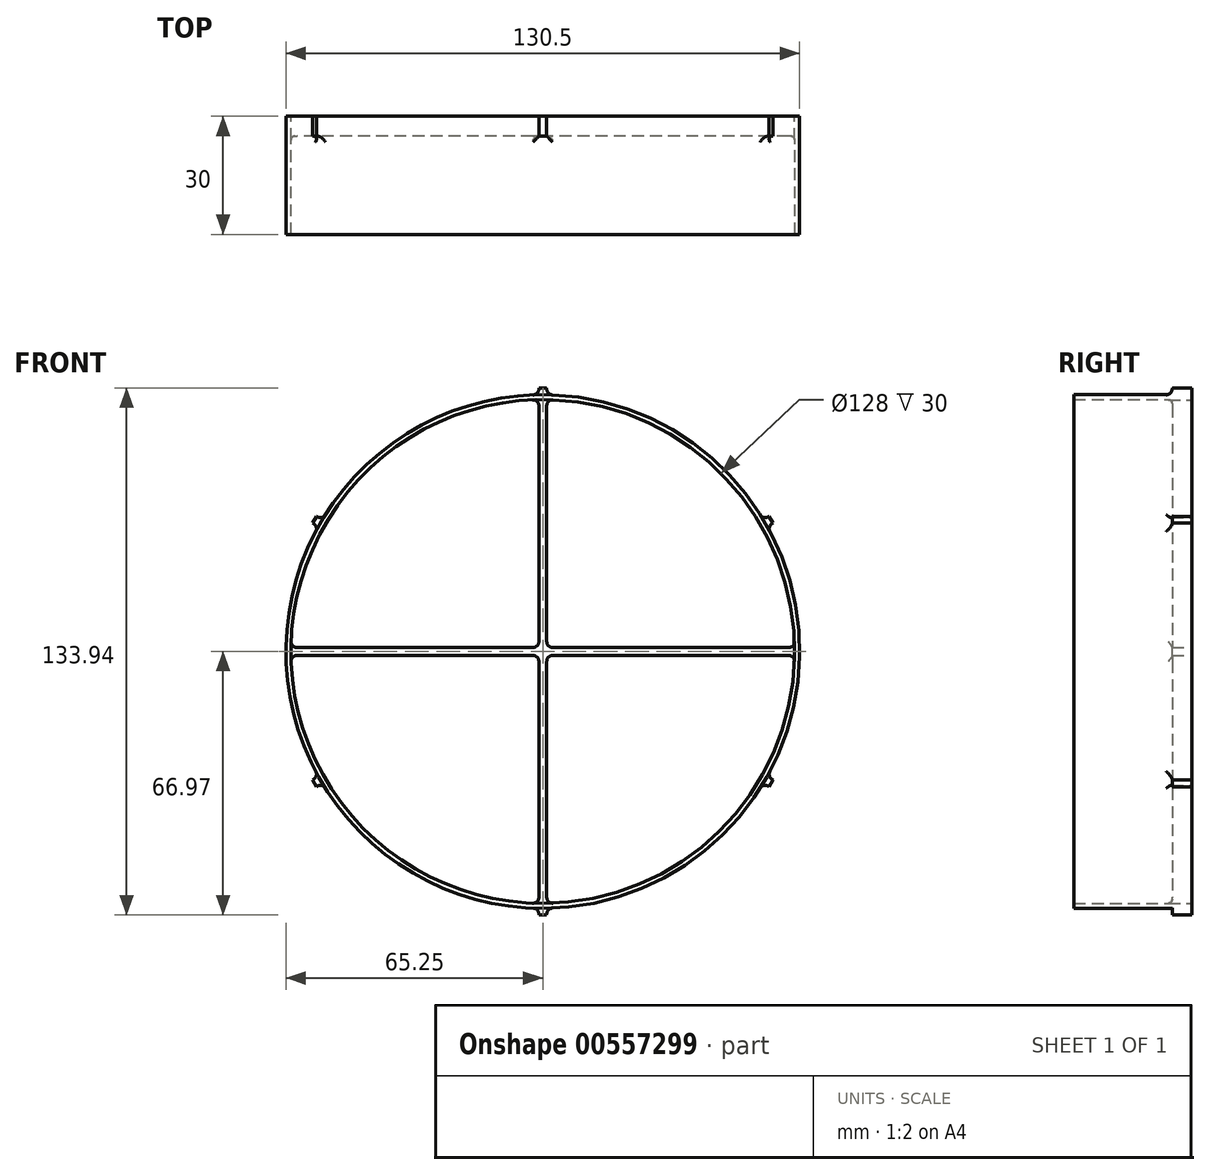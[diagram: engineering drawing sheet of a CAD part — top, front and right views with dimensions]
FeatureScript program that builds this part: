
annotation { "Feature Type Name" : "Feature", "Feature Type Description" : "" }
export const myFeature = defineFeature(function(context is Context, id is Id, definition is map)
    precondition{}
    {
        {
            var Q0;
            Q0=qCreatedBy(makeId("Front.planeOp"),FACE);
            var sketch = newSketch(context, id + "F0", { "sketchPlane" : qUnion([Q0])});
            skArc(sketch, "E0", {"start": v(64, 1) * mm, "mid": v(45.25, 45.25) * mm, "end": v(1, 64) * mm});
            skCircle(sketch, "E1", {"center": v(0, 0) * mm, "radius": 65.25 * mm});
            skLineSegment(sketch, "E2", {"start": v(0, 0) * mm, "end": v(0, 65.25) * mm, "construction": true});
            skLineSegment(sketch, "E3", {"start": v(0, 65.25) * mm, "end": v(0, -65.25) * mm, "construction": true});
            skLineSegment(sketch, "E4", {"start": v(0, -65.25) * mm, "end": v(0, 0) * mm, "construction": true});
            skLineSegment(sketch, "E5", {"start": v(65.25, 0) * mm, "end": v(-65.25, 0) * mm, "construction": true});
            skLineSegment(sketch, "E6.0", {"start": v(66, 1) * mm, "end": v(65.24, 1) * mm});
            skLineSegment(sketch, "E7.0", {"start": v(66, -1) * mm, "end": v(65.24, -1) * mm});
            skLineSegment(sketch, "E8.trimOffspring", {"start": v(-1, -1) * mm, "end": v(-1, -64) * mm});
            skLineSegment(sketch, "E9.trimOffspring", {"start": v(-1, 1) * mm, "end": v(-64, 1) * mm});
            skLineSegment(sketch, "E10.trimOffspring", {"start": v(1, -1) * mm, "end": v(1, -64) * mm});
            skLineSegment(sketch, "E11.trimOffspring", {"start": v(-1, -1) * mm, "end": v(-64, -1) * mm});
            skLineSegment(sketch, "E12.trimOffspring", {"start": v(64, 1) * mm, "end": v(1, 1) * mm});
            skLineSegment(sketch, "E13.trimOffspring", {"start": v(64, -1) * mm, "end": v(1, -1) * mm});
            skArc(sketch, "E14.trimOffspring", {"start": v(-1, 64) * mm, "mid": v(-45.25, 45.25) * mm, "end": v(-64, 1) * mm});
            skLineSegment(sketch, "E15.trimOffspring", {"start": v(1, 64) * mm, "end": v(1, 1) * mm});
            skLineSegment(sketch, "E16.trimOffspring", {"start": v(-1, 64) * mm, "end": v(-1, 1) * mm});
            skArc(sketch, "E17.trimOffspring", {"start": v(-64, -1) * mm, "mid": v(-45.25, -45.25) * mm, "end": v(-1, -64) * mm});
            skLineSegment(sketch, "E18.trimOffspring", {"start": v(-65.24, 1) * mm, "end": v(-66, 1) * mm});
            skLineSegment(sketch, "E19.trimOffspring", {"start": v(-65.24, -1) * mm, "end": v(-66, -1) * mm});
            skArc(sketch, "E20.trimOffspring", {"start": v(1, -64) * mm, "mid": v(45.25, -45.25) * mm, "end": v(64, -1) * mm});
            skLineSegment(sketch, "E21.trimOffspring", {"start": v(1, -65.24) * mm, "end": v(1, -66) * mm});
            skLineSegment(sketch, "E22.trimOffspring", {"start": v(-1, -65.24) * mm, "end": v(-1, -66) * mm});
            skLineSegment(sketch, "E23.bottom", {"start": v(-1, 64.97) * mm, "end": v(1, 64.97) * mm});
            skLineSegment(sketch, "E23.top", {"start": v(-1, 66.97) * mm, "end": v(1, 66.97) * mm});
            skLineSegment(sketch, "E23.left", {"start": v(-1, 64.97) * mm, "end": v(-1, 66.97) * mm});
            skLineSegment(sketch, "E23.right", {"start": v(1, 64.97) * mm, "end": v(1, 66.97) * mm});
            skLineSegment(sketch, "E24.1.0", {"start": v(-56.77, -31.62) * mm, "end": v(-58.5, -32.62) * mm});
            skLineSegment(sketch, "E24.1.1", {"start": v(-55.77, -33.35) * mm, "end": v(-56.77, -31.62) * mm});
            skLineSegment(sketch, "E24.1.2", {"start": v(-55.77, -33.35) * mm, "end": v(-57.5, -34.35) * mm});
            skLineSegment(sketch, "E24.1.3", {"start": v(-57.5, -34.35) * mm, "end": v(-58.5, -32.62) * mm});
            skLineSegment(sketch, "E24.2.0", {"start": v(55.77, -33.35) * mm, "end": v(57.5, -34.35) * mm});
            skLineSegment(sketch, "E24.2.1", {"start": v(56.77, -31.62) * mm, "end": v(55.77, -33.35) * mm});
            skLineSegment(sketch, "E24.2.2", {"start": v(56.77, -31.62) * mm, "end": v(58.5, -32.62) * mm});
            skLineSegment(sketch, "E24.2.3", {"start": v(58.5, -32.62) * mm, "end": v(57.5, -34.35) * mm});
            skLineSegment(sketch, "E25.1.0", {"start": v(-55.77, 33.35) * mm, "end": v(-57.5, 34.35) * mm});
            skLineSegment(sketch, "E25.1.1", {"start": v(-56.77, 31.62) * mm, "end": v(-55.77, 33.35) * mm});
            skLineSegment(sketch, "E25.1.2", {"start": v(-58.5, 32.62) * mm, "end": v(-57.5, 34.35) * mm});
            skLineSegment(sketch, "E25.1.3", {"start": v(-56.77, 31.62) * mm, "end": v(-58.5, 32.62) * mm});
            skLineSegment(sketch, "E25.3.0", {"start": v(-1, -64.97) * mm, "end": v(-1, -66.97) * mm});
            skLineSegment(sketch, "E25.3.1", {"start": v(1, -64.97) * mm, "end": v(-1, -64.97) * mm});
            skLineSegment(sketch, "E25.3.2", {"start": v(1, -66.97) * mm, "end": v(-1, -66.97) * mm});
            skLineSegment(sketch, "E25.3.3", {"start": v(1, -64.97) * mm, "end": v(1, -66.97) * mm});
            skLineSegment(sketch, "E25.5.0", {"start": v(56.77, 31.62) * mm, "end": v(58.5, 32.62) * mm});
            skLineSegment(sketch, "E25.5.1", {"start": v(55.77, 33.35) * mm, "end": v(56.77, 31.62) * mm});
            skLineSegment(sketch, "E25.5.2", {"start": v(57.5, 34.35) * mm, "end": v(58.5, 32.62) * mm});
            skLineSegment(sketch, "E25.5.3", {"start": v(55.77, 33.35) * mm, "end": v(57.5, 34.35) * mm});
            skSolve(sketch);
        }
        {
            var Q0;
            Q0 = qSketchRegion(id + "F0", true);
            extrude(context, id + "F1", {"entities" : qUnion([Q0]), "depth" : 5 * mm, "offsetDistance" : 25 * mm});
        }
        {
            var Q0;
            Q0=makeQuery(id+"F1.opExtrude","SWEPT_EDGE",EDGE,{"disambiguationData":[OSD([sQuery(id+"F0.wireOp",EDGE,"E13.trimOffspring"),sQuery(id+"F0.wireOp",EDGE,"E20.trimOffspring")])]});
            var Q1;
            Q1=makeQuery(id+"F1.opExtrude","SWEPT_EDGE",EDGE,{"disambiguationData":[OSD([sQuery(id+"F0.wireOp",EDGE,"E0"),sQuery(id+"F0.wireOp",EDGE,"E12.trimOffspring")])]});
            var Q2;
            Q2=makeQuery(id+"F1.opExtrude","SWEPT_EDGE",EDGE,{"disambiguationData":[OSD([sQuery(id+"F0.wireOp",EDGE,"E8.trimOffspring"),sQuery(id+"F0.wireOp",EDGE,"E17.trimOffspring")])]});
            var Q3;
            Q3=makeQuery(id+"F1.opExtrude","SWEPT_EDGE",EDGE,{"disambiguationData":[OSD([sQuery(id+"F0.wireOp",EDGE,"E10.trimOffspring"),sQuery(id+"F0.wireOp",EDGE,"E20.trimOffspring")])]});
            var Q4;
            Q4=makeQuery(id+"F1.opExtrude","SWEPT_EDGE",EDGE,{"disambiguationData":[OSD([sQuery(id+"F0.wireOp",EDGE,"E9.trimOffspring"),sQuery(id+"F0.wireOp",EDGE,"E14.trimOffspring")])]});
            var Q5;
            Q5=makeQuery(id+"F1.opExtrude","SWEPT_EDGE",EDGE,{"disambiguationData":[OSD([sQuery(id+"F0.wireOp",EDGE,"E11.trimOffspring"),sQuery(id+"F0.wireOp",EDGE,"E17.trimOffspring")])]});
            var Q6;
            Q6=makeQuery(id+"F1.opExtrude","SWEPT_EDGE",EDGE,{"disambiguationData":[OSD([sQuery(id+"F0.wireOp",EDGE,"E0"),sQuery(id+"F0.wireOp",EDGE,"E15.trimOffspring")])]});
            var Q7;
            Q7=makeQuery(id+"F1.opExtrude","SWEPT_EDGE",EDGE,{"disambiguationData":[OSD([sQuery(id+"F0.wireOp",EDGE,"E14.trimOffspring"),sQuery(id+"F0.wireOp",EDGE,"E16.trimOffspring")])]});
            fillet(context, id + "F2", {"entities" : qUnion([Q0, Q1, Q2, Q3, Q4, Q5, Q6, Q7]), "radius" : 1.5 * mm, "tangentPropagation" : true, "allowEdgeOverflow" : false});
        }
        {
            var Q0;
            Q0=makeQuery(id+"F1.opExtrude","SWEPT_EDGE",EDGE,{"disambiguationData":[OSD([sQuery(id+"F0.wireOp",EDGE,"E8.trimOffspring"),sQuery(id+"F0.wireOp",EDGE,"E11.trimOffspring")])]});
            var Q1;
            Q1=makeQuery(id+"F1.opExtrude","SWEPT_EDGE",EDGE,{"disambiguationData":[OSD([sQuery(id+"F0.wireOp",EDGE,"E10.trimOffspring"),sQuery(id+"F0.wireOp",EDGE,"E13.trimOffspring")])]});
            var Q2;
            Q2=makeQuery(id+"F1.opExtrude","SWEPT_EDGE",EDGE,{"disambiguationData":[OSD([sQuery(id+"F0.wireOp",EDGE,"E12.trimOffspring"),sQuery(id+"F0.wireOp",EDGE,"E15.trimOffspring")])]});
            var Q3;
            Q3=makeQuery(id+"F1.opExtrude","SWEPT_EDGE",EDGE,{"disambiguationData":[OSD([sQuery(id+"F0.wireOp",EDGE,"E9.trimOffspring"),sQuery(id+"F0.wireOp",EDGE,"E16.trimOffspring")])]});
            fillet(context, id + "F3", {"entities" : qUnion([Q0, Q1, Q2, Q3]), "radius" : 1.5 * mm, "tangentPropagation" : true, "allowEdgeOverflow" : false});
        }
        {
            var Q0;
            Q0=makeQuery(id+"F1.opExtrude","CAP_FACE",FACE,{"disambiguationData":[OSD([sQuery(id+"F0.wireOp",EDGE,"E0"),sQuery(id+"F0.wireOp",EDGE,"E1"),sQuery(id+"F0.wireOp",EDGE,"E8.trimOffspring"),sQuery(id+"F0.wireOp",EDGE,"E9.trimOffspring"),sQuery(id+"F0.wireOp",EDGE,"E10.trimOffspring"),sQuery(id+"F0.wireOp",EDGE,"E11.trimOffspring"),sQuery(id+"F0.wireOp",EDGE,"E12.trimOffspring"),sQuery(id+"F0.wireOp",EDGE,"E13.trimOffspring"),sQuery(id+"F0.wireOp",EDGE,"E14.trimOffspring"),sQuery(id+"F0.wireOp",EDGE,"E15.trimOffspring"),sQuery(id+"F0.wireOp",EDGE,"E16.trimOffspring"),sQuery(id+"F0.wireOp",EDGE,"E17.trimOffspring"),sQuery(id+"F0.wireOp",EDGE,"E20.trimOffspring")])],"isStart":false});
            var sketch = newSketch(context, id + "F4", { "sketchPlane" : qUnion([Q0])});
            skCircle(sketch, "E26", {"center": v(0, 0) * mm, "radius": 64 * mm});
            skCircle(sketch, "E27", {"center": v(0, 0) * mm, "radius": 65.25 * mm});
            skSolve(sketch);
        }
        {
            var Q0;
            Q0 = qSketchRegion(id + "F4", true);
            extrude(context, id + "F5", {"entities" : qUnion([Q0]), "operationType" : NewBodyOperationType.ADD, "depth" : 25 * mm, "offsetDistance" : 25 * mm});
        }
        {
            var Q0;
            {var subQ3=sQuery(id+"F0.wireOp",EDGE,"E15.trimOffspring");var subQ5=sQuery(id+"F0.wireOp",EDGE,"E0");var subQ6=sQuery(id+"F4.wireOp",EDGE,"E26");Q0=makeQuery(id+"F5.boolean.opBoolean","SPLIT",EDGE,{"disambiguationData":[TD([makeQuery(id+"F2.opFillet","BLEND_FACE",FACE,{"disambiguationData":[OSD([subQ5,subQ3])]})])],"derivedFrom":makeQuery(id+"F5.opExtrude","CAP_EDGE",EDGE,{"disambiguationData":[OSD([subQ6])],"isStart":true})});}
            var Q1;
            {var subQ4=sQuery(id+"F0.wireOp",EDGE,"E12.trimOffspring");var subQ5=sQuery(id+"F0.wireOp",EDGE,"E0");var subQ6=sQuery(id+"F4.wireOp",EDGE,"E26");Q1=makeQuery(id+"F5.boolean.opBoolean","SPLIT",EDGE,{"disambiguationData":[TD([makeQuery(id+"F2.opFillet","BLEND_FACE",FACE,{"disambiguationData":[OSD([subQ5,subQ4])]})])],"derivedFrom":makeQuery(id+"F5.opExtrude","CAP_EDGE",EDGE,{"disambiguationData":[OSD([subQ6])],"isStart":true})});}
            var Q2;
            {var subQ2=sQuery(id+"F0.wireOp",EDGE,"E14.trimOffspring");var subQ4=sQuery(id+"F0.wireOp",EDGE,"E9.trimOffspring");var subQ6=sQuery(id+"F4.wireOp",EDGE,"E26");Q2=makeQuery(id+"F5.boolean.opBoolean","SPLIT",EDGE,{"disambiguationData":[TD([makeQuery(id+"F2.opFillet","BLEND_FACE",FACE,{"disambiguationData":[OSD([subQ4,subQ2])]})])],"derivedFrom":makeQuery(id+"F5.opExtrude","CAP_EDGE",EDGE,{"disambiguationData":[OSD([subQ6])],"isStart":true})});}
            var Q3;
            {var subQ0=sQuery(id+"F0.wireOp",EDGE,"E17.trimOffspring");var subQ4=sQuery(id+"F0.wireOp",EDGE,"E8.trimOffspring");var subQ6=sQuery(id+"F4.wireOp",EDGE,"E26");Q3=makeQuery(id+"F5.boolean.opBoolean","SPLIT",EDGE,{"disambiguationData":[TD([makeQuery(id+"F2.opFillet","BLEND_FACE",FACE,{"disambiguationData":[OSD([subQ4,subQ0])]})])],"derivedFrom":makeQuery(id+"F5.opExtrude","CAP_EDGE",EDGE,{"disambiguationData":[OSD([subQ6])],"isStart":true})});}
            fillet(context, id + "F6", {"entities" : qUnion([Q0, Q1, Q2, Q3]), "radius" : 1 * mm, "tangentPropagation" : true, "allowEdgeOverflow" : false});
        }
        {
            var Q0;
            Q0=makeQuery(id+"F1.opExtrude","SWEPT_EDGE",EDGE,{"disambiguationData":[OSD([sQuery(id+"F0.wireOp",EDGE,"E1"),sQuery(id+"F0.wireOp",EDGE,"E23.left")])]});
            var Q1;
            Q1=makeQuery(id+"F1.opExtrude","SWEPT_EDGE",EDGE,{"disambiguationData":[OSD([sQuery(id+"F0.wireOp",EDGE,"E1"),sQuery(id+"F0.wireOp",EDGE,"E23.right")])]});
            var Q2;
            Q2=makeQuery(id+"F1.opExtrude","SWEPT_EDGE",EDGE,{"disambiguationData":[OSD([sQuery(id+"F0.wireOp",EDGE,"E1"),sQuery(id+"F0.wireOp",EDGE,"E25.5.0")])]});
            var Q3;
            Q3=makeQuery(id+"F1.opExtrude","SWEPT_EDGE",EDGE,{"disambiguationData":[OSD([sQuery(id+"F0.wireOp",EDGE,"E1"),sQuery(id+"F0.wireOp",EDGE,"E25.5.3")])]});
            var Q4;
            Q4=makeQuery(id+"F1.opExtrude","SWEPT_EDGE",EDGE,{"disambiguationData":[OSD([sQuery(id+"F0.wireOp",EDGE,"E1"),sQuery(id+"F0.wireOp",EDGE,"E24.2.0")])]});
            var Q5;
            Q5=makeQuery(id+"F1.opExtrude","SWEPT_EDGE",EDGE,{"disambiguationData":[OSD([sQuery(id+"F0.wireOp",EDGE,"E1"),sQuery(id+"F0.wireOp",EDGE,"E24.2.2")])]});
            var Q6;
            Q6=makeQuery(id+"F1.opExtrude","SWEPT_EDGE",EDGE,{"disambiguationData":[OSD([sQuery(id+"F0.wireOp",EDGE,"E1"),sQuery(id+"F0.wireOp",EDGE,"E25.3.3")])]});
            var Q7;
            Q7=makeQuery(id+"F1.opExtrude","SWEPT_EDGE",EDGE,{"disambiguationData":[OSD([sQuery(id+"F0.wireOp",EDGE,"E1"),sQuery(id+"F0.wireOp",EDGE,"E25.3.0")])]});
            var Q8;
            Q8=makeQuery(id+"F1.opExtrude","SWEPT_EDGE",EDGE,{"disambiguationData":[OSD([sQuery(id+"F0.wireOp",EDGE,"E1"),sQuery(id+"F0.wireOp",EDGE,"E24.1.2")])]});
            var Q9;
            Q9=makeQuery(id+"F1.opExtrude","SWEPT_EDGE",EDGE,{"disambiguationData":[OSD([sQuery(id+"F0.wireOp",EDGE,"E1"),sQuery(id+"F0.wireOp",EDGE,"E24.1.0")])]});
            var Q10;
            Q10=makeQuery(id+"F1.opExtrude","SWEPT_EDGE",EDGE,{"disambiguationData":[OSD([sQuery(id+"F0.wireOp",EDGE,"E1"),sQuery(id+"F0.wireOp",EDGE,"E25.1.0")])]});
            var Q11;
            Q11=makeQuery(id+"F1.opExtrude","SWEPT_EDGE",EDGE,{"disambiguationData":[OSD([sQuery(id+"F0.wireOp",EDGE,"E1"),sQuery(id+"F0.wireOp",EDGE,"E25.1.3")])]});
            var Q12;
            {var subQ11=sQuery(id+"F0.wireOp",EDGE,"E25.3.0");var subQ17=sQuery(id+"F4.wireOp",EDGE,"E27");Q12=makeQuery(id+"F5.boolean.opBoolean","SPLIT",EDGE,{"disambiguationData":[TD([makeQuery(id+"F1.opExtrude","SWEPT_FACE",FACE,{"disambiguationData":[OSD([subQ11])]})])],"derivedFrom":makeQuery(id+"F5.opExtrude","CAP_EDGE",EDGE,{"disambiguationData":[OSD([subQ17])],"isStart":true})});}
            var Q13;
            {var subQ9=sQuery(id+"F0.wireOp",EDGE,"E24.2.0");var subQ17=sQuery(id+"F4.wireOp",EDGE,"E27");Q13=makeQuery(id+"F5.boolean.opBoolean","SPLIT",EDGE,{"disambiguationData":[TD([makeQuery(id+"F1.opExtrude","SWEPT_FACE",FACE,{"disambiguationData":[OSD([subQ9])]})])],"derivedFrom":makeQuery(id+"F5.opExtrude","CAP_EDGE",EDGE,{"disambiguationData":[OSD([subQ17])],"isStart":true})});}
            var Q14;
            {var subQ8=sQuery(id+"F0.wireOp",EDGE,"E25.5.0");var subQ17=sQuery(id+"F4.wireOp",EDGE,"E27");Q14=makeQuery(id+"F5.boolean.opBoolean","SPLIT",EDGE,{"disambiguationData":[TD([makeQuery(id+"F1.opExtrude","SWEPT_FACE",FACE,{"disambiguationData":[OSD([subQ8])]})])],"derivedFrom":makeQuery(id+"F5.opExtrude","CAP_EDGE",EDGE,{"disambiguationData":[OSD([subQ17])],"isStart":true})});}
            var Q15;
            {var subQ0=sQuery(id+"F0.wireOp",EDGE,"E23.left");var subQ17=sQuery(id+"F4.wireOp",EDGE,"E27");Q15=makeQuery(id+"F5.boolean.opBoolean","SPLIT",EDGE,{"disambiguationData":[TD([makeQuery(id+"F1.opExtrude","SWEPT_FACE",FACE,{"disambiguationData":[OSD([subQ0])]})])],"derivedFrom":makeQuery(id+"F5.opExtrude","CAP_EDGE",EDGE,{"disambiguationData":[OSD([subQ17])],"isStart":true})});}
            var Q16;
            {var subQ2=sQuery(id+"F0.wireOp",EDGE,"E25.1.0");var subQ17=sQuery(id+"F4.wireOp",EDGE,"E27");Q16=makeQuery(id+"F5.boolean.opBoolean","SPLIT",EDGE,{"disambiguationData":[TD([makeQuery(id+"F1.opExtrude","SWEPT_FACE",FACE,{"disambiguationData":[OSD([subQ2])]})])],"derivedFrom":makeQuery(id+"F5.opExtrude","CAP_EDGE",EDGE,{"disambiguationData":[OSD([subQ17])],"isStart":true})});}
            var Q17;
            {var subQ5=sQuery(id+"F0.wireOp",EDGE,"E24.1.0");var subQ17=sQuery(id+"F4.wireOp",EDGE,"E27");Q17=makeQuery(id+"F5.boolean.opBoolean","SPLIT",EDGE,{"disambiguationData":[TD([makeQuery(id+"F1.opExtrude","SWEPT_FACE",FACE,{"disambiguationData":[OSD([subQ5])]})])],"derivedFrom":makeQuery(id+"F5.opExtrude","CAP_EDGE",EDGE,{"disambiguationData":[OSD([subQ17])],"isStart":true})});}
            fillet(context, id + "F7", {"entities" : qUnion([Q0, Q1, Q2, Q3, Q4, Q5, Q6, Q7, Q8, Q9, Q10, Q11, Q12, Q13, Q14, Q15, Q16, Q17]), "radius" : 1.5 * mm, "tangentPropagation" : true, "allowEdgeOverflow" : false});
        }
    });
